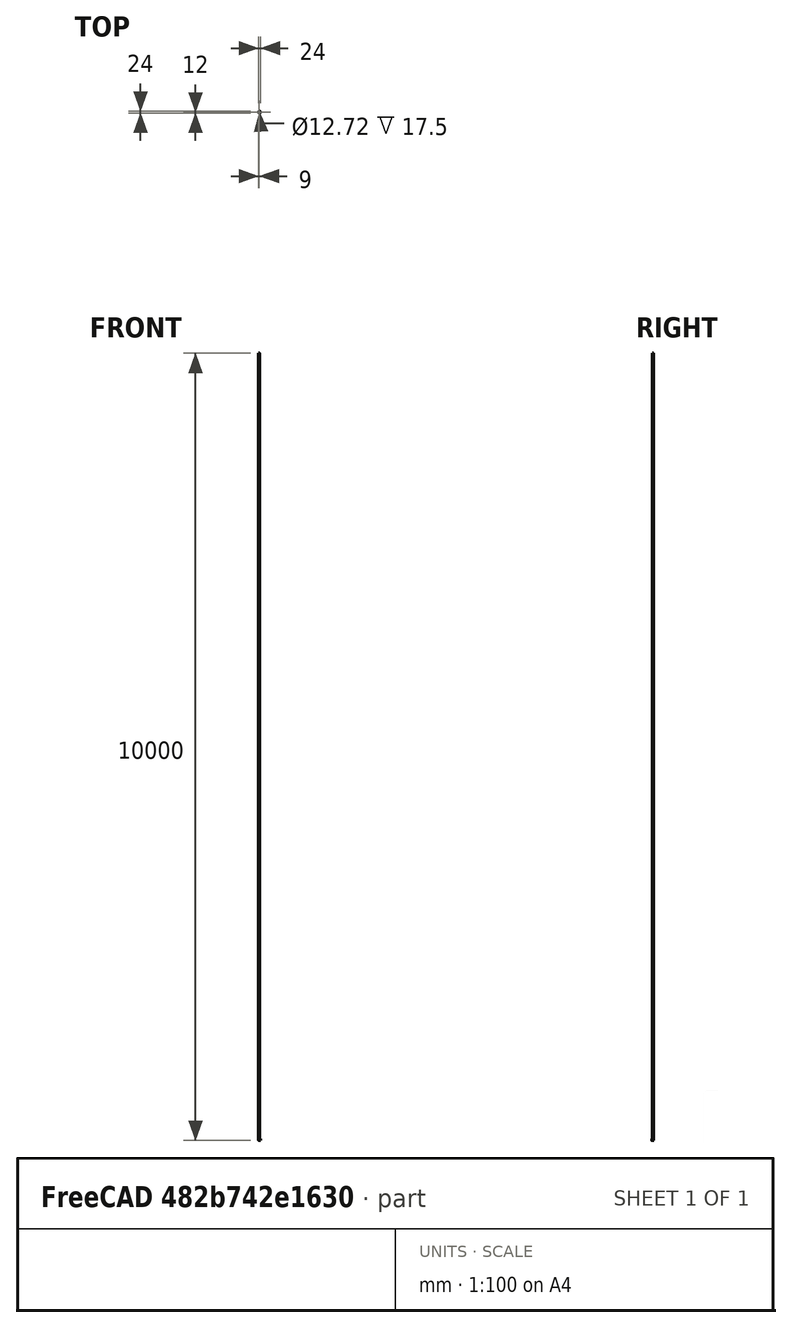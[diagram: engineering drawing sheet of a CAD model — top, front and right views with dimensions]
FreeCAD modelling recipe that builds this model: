
FCSTD DOCUMENT  (FreeCAD 0.16R)
Label: LeverEcc22
License: All rights reserved
LicenseURL: http://en.wikipedia.org/wiki/All_rights_reserved
objects: Sketcher::SketchObject×5, PartDesign::Chamfer×5, PartDesign::Pad×3, PartDesign::Pocket×2, Mesh::Feature×1
note: 20 computed .brp shape members not serialized (recipe doc carries the construction recipe); baked Part::Feature solids carry a one-line shape summary decoded from their .brp

FEATURE [Sketcher::SketchObject] Sketch
  sketch-geometry (1):
    g0: Circle CenterX=0 CenterY=0 CenterZ=0 NormalX=0 NormalY=0 NormalZ=1 Radius=11
  constraints (2):
    c: Coincident(g0,g-1)
    c: Radius(g0) = 11
FEATURE [PartDesign::Pad] Pad
  Length = 15.5
  Length2 = 100
  Sketch = -> Sketch
  Type = 0
FEATURE [Sketcher::SketchObject] Sketch002
  Placement = pos=(0,0,15.5) rot=(0,0,1;0rad)
  Support = -> Pad [Face3]
  sketch-geometry (1):
    g0: Circle CenterX=0 CenterY=0 CenterZ=0 NormalX=0 NormalY=0 NormalZ=1 Radius=12
  constraints (2):
    c: Radius(g0) = 12
    c: Coincident(g0,g-1)
FEATURE [PartDesign::Pad] Pad001
  Length = 1
  Length2 = 100
  Sketch = -> Sketch002
  Type = 0
FEATURE [Sketcher::SketchObject] Sketch005
  Placement = pos=(0,0,0) rot=(1,0,0;3.14159rad)
  Support = -> Pad001 [Face1]
  sketch-geometry (1):
    g0: Circle CenterX=0 CenterY=0 CenterZ=0 NormalX=0 NormalY=0 NormalZ=1 Radius=12
  constraints (2):
    c: Coincident(g0,g-1)
    c: Radius(g0) = 12
FEATURE [PartDesign::Pad] Pad002
  Length = 1
  Length2 = 100
  Sketch = -> Sketch005
  Type = 0
FEATURE [Sketcher::SketchObject] Sketch003
  Placement = pos=(0,0,-1) rot=(1,0,0;3.14159rad)
  Support = -> Pad002 [Face7]
  sketch-geometry (1):
    g0: Circle CenterX=-3 CenterY=0 CenterZ=0 NormalX=0 NormalY=0 NormalZ=1 Radius=6.36
  constraints (3):
    c: Radius(g0) = 6.36
    c: PointOnObject(g0,g-1)
    c: DistanceX(g0) = -3
FEATURE [PartDesign::Pocket] Pocket
  Length = 5
  Sketch = -> Sketch003
  Type = 1
FEATURE [Sketcher::SketchObject] Sketch004
  Placement = pos=(0,0,-1) rot=(1,0,0;3.14159rad)
  Support = -> Pocket [Face8]
  sketch-geometry (4):
    g0: LineSegment StartX=-15.5366 StartY=1 StartZ=0 EndX=14.4634 EndY=1 EndZ=0
    g1: LineSegment StartX=14.4634 StartY=1 StartZ=0 EndX=14.4634 EndY=-1 EndZ=0
    g2: LineSegment StartX=14.4634 StartY=-1 StartZ=0 EndX=-15.5366 EndY=-1 EndZ=0
    g3: LineSegment StartX=-15.5366 StartY=-1 StartZ=0 EndX=-15.5366 EndY=1 EndZ=0
  constraints (11):
    c: Coincident(g0,g1)
    c: Coincident(g2,g3)
    c: Coincident(g3,g0)
    c: Horizontal(g0)
    c: Horizontal(g2)
    c: Vertical(g1)
    c: Vertical(g3)
    c: Distance(g1) = 2
    c: Symmetric(g2,g0,g-1)
    c: Distance(g0) = 30
    c: Distance(g3) = 2
FEATURE [PartDesign::Pocket] Pocket001
  Length = 17.4
  Sketch = -> Sketch004
  Type = 0
FEATURE [PartDesign::Chamfer] Chamfer
  Base = -> Pocket001 [Edge21,Edge34,Edge18,Edge42,Edge20,Edge40,Edge24,Edge36]
  Size = 1
FEATURE [PartDesign::Chamfer] Chamfer001
  Base = -> Chamfer [Edge33,Edge29]
  Size = 1
FEATURE [PartDesign::Chamfer] Chamfer002
  Base = -> Chamfer001 [Edge27,Edge22]
  Size = 1
FEATURE [PartDesign::Chamfer] Chamfer003
  Base = -> Chamfer002 [Edge11,Edge100]
  Size = 0.9
FEATURE [PartDesign::Chamfer] Chamfer004
  Base = -> Chamfer003 [Edge101,Edge10]
  Size = 0.9
FEATURE [Mesh::Feature] Mesh  label="Chamfer004 (Meshed)"
